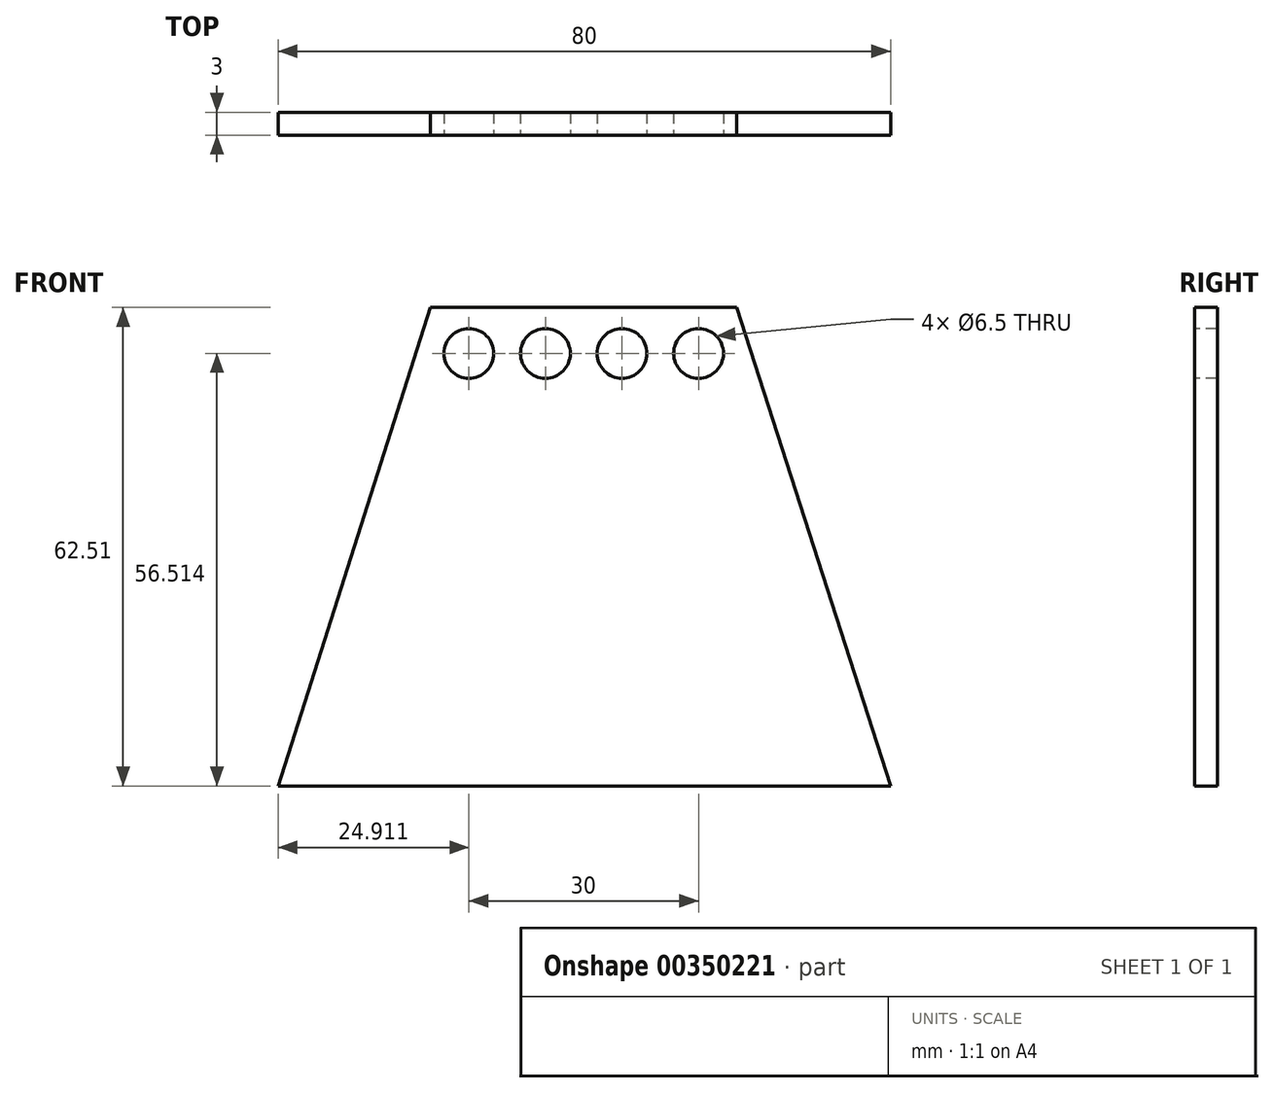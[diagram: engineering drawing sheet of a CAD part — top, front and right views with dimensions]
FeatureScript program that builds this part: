
annotation { "Feature Type Name" : "Feature", "Feature Type Description" : "" }
export const myFeature = defineFeature(function(context is Context, id is Id, definition is map)
    precondition{}
    {
        {
            var Q0;
            Q0=qCreatedBy(makeId("Front.planeOp"),FACE);
            var sketch = newSketch(context, id + "F0", { "sketchPlane" : qUnion([Q0])});
            skLineSegment(sketch, "E0", {"start": v(-18.59, 30.37) * mm, "end": v(21.41, 30.37) * mm});
            skLineSegment(sketch, "E1", {"start": v(21.41, 30.37) * mm, "end": v(41.5, -32.14) * mm});
            skLineSegment(sketch, "E2", {"start": v(41.5, -32.14) * mm, "end": v(-38.5, -32.14) * mm});
            skLineSegment(sketch, "E3", {"start": v(-38.5, -32.14) * mm, "end": v(-18.59, 30.37) * mm});
            skSolve(sketch);
        }
        {
            var Q0;
            Q0 = qSketchRegion(id + "F0", true);
            extrude(context, id + "F1", {"entities" : qUnion([Q0]), "depth" : 3 * mm});
        }
        {
            var Q0;
            Q0=makeQuery(id+"F1.opExtrude","CAP_FACE",FACE,{"disambiguationData":[OSD([sQuery(id+"F0.wireOp",EDGE,"E0"),sQuery(id+"F0.wireOp",EDGE,"E1"),sQuery(id+"F0.wireOp",EDGE,"E2"),sQuery(id+"F0.wireOp",EDGE,"E3")])],"isStart":false});
            var sketch = newSketch(context, id + "F2", { "sketchPlane" : qUnion([Q0])});
            skCircle(sketch, "E4", {"center": v(-13.59, 24.37) * mm, "radius": 3.25 * mm});
            skCircle(sketch, "E5", {"center": v(-3.59, 24.37) * mm, "radius": 3.25 * mm});
            skCircle(sketch, "E6", {"center": v(6.41, 24.37) * mm, "radius": 3.25 * mm});
            skCircle(sketch, "E7", {"center": v(16.41, 24.37) * mm, "radius": 3.25 * mm});
            skSolve(sketch);
        }
        {
            var Q0;
            Q0 = qSketchRegion(id + "F2", true);
            extrude(context, id + "F3", {"entities" : qUnion([Q0]), "operationType" : NewBodyOperationType.REMOVE, "endBound" : BoundingType.THROUGH_ALL, "oppositeDirection" : true, "depth" : 25 * mm});
        }
    });
